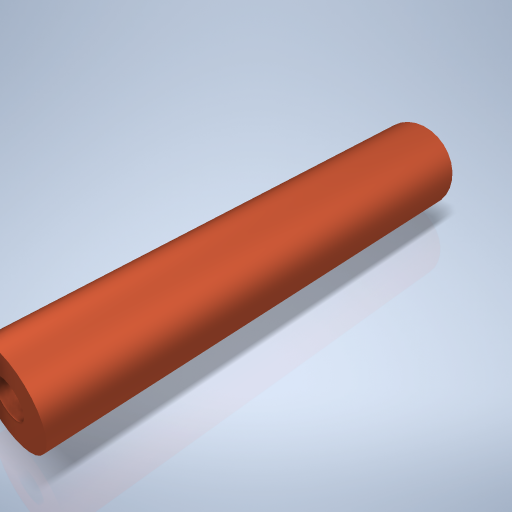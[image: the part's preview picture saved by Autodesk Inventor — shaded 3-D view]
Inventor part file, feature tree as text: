
AUTODESK INVENTOR PART (.ipt)
format: ipt  version: 2024.2 (Build 282272000, 272)  size: 251,904 bytes
history: native  units: mm
features: extrude x2, sketch x2, chamfer x1
ambient origin geometry x8: Origin, YZ Plane, XZ Plane, XY Plane, X Axis, Y Axis, Z Axis, Center Point
bodies: Volumenkörper1 (feature_tree)
feature tree (5):
  extrude  "Extrusion1"  Depth=160.0mm TaperAngle=0.0deg
  chamfer  "Fasen1"  Distance=4.0mm Angle=45.0deg
  extrude  "Extrusion2"  Depth=160.0mm TaperAngle=0.0deg
  sketch  "Skizze1"  dims[d0=30.0mm d1=160.0mm d2=0.0mm d3=4.0mm d4=2.0mm d5=45.0deg]
  sketch  "Skizze2"  dims[d6=12.5mm d7=160.0mm d8=0.0mm d9=0.5mm d10=0.872665mm d11=0.5mm d12=0.872665mm]
